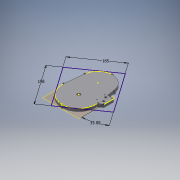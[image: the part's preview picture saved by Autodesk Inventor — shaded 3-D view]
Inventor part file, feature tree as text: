
AUTODESK INVENTOR PART (.ipt)
format: ipt  version: 2017 (Build 210142000, 142)  size: 453,632 bytes
history: native  units: mm
features: extrude x9, sketch x9, other x7, projected_geometry x6, reference x4, plane x2
ambient origin geometry x8: Origin, YZ Plane, XZ Plane, XY Plane, X Axis, Y Axis, Z Axis, Center Point
bodies: Solid1 (feature_tree)
feature tree (37):
  plane  "Work Plane1"
  extrude  "Extrusion1"  Depth=55.0mm
  extrude  "Extrusion2"  Depth=10.0mm TaperAngle=0.0deg
  extrude  "Extrusion3"  Depth=2.0mm TaperAngle=0.0deg
  extrude  "Extrusion5"  Depth=80.0mm
  extrude  "Extrusion6"  Depth=8.0mm
  sketch  "Sketch7"  dims[d12=40.0mm d13=12.0mm]
  extrude  "Extrusion7"  Depth=12.0mm
  extrude  "Extrusion8"  Depth=10.0mm TaperAngle=0.0deg
  extrude  "Extrusion9"  Depth=10.0mm
  sketch  "Sketch9"  dims[d24=10.0mm d25=0.0mm d26=3.81mm]
  plane  "Work Plane2"
  extrude  "Extrusion10"  Depth=10.0mm TaperAngle=0.0deg
  sketch  "Sketch10"  dims[d27=8.0mm d28=10.0mm d29=0.0mm d30=10.0mm d31=0.0mm d32=2.794mm d33=4.0mm d34=33.0mm d35=28.0mm d36=10.0mm d37=0.0mm d38=30.0deg d39=10.0mm d40=0.0mm d41=198.0mm d42=185.0mm d43=6.108652mm d44=13.5mm]
  sketch  "Sketch1"  dims[d0=65.0mm d1=55.0mm]
  reference  "Reference1"
  reference  "Reference2"
  reference  "Reference3"
  reference  "Reference4"
  sketch  "Sketch2"  dims[d2=5.0mm d3=10.0mm d4=0.0mm]
  projected_geometry  "Projected Loop1"
  sketch  "Sketch3"  dims[d5=13.5mm d6=2.0mm d7=0.0mm]
  projected_geometry  "Projected Loop2"
  sketch  "Sketch5"  dims[d8=80.0mm d9=20.0mm]
  sketch  "Sketch6"  dims[d10=3.490659mm d11=8.0mm]
  projected_geometry  "Projected Loop3"
  projected_geometry  "Projected Loop4"
  sketch  "Sketch8"  dims[d14=10.0mm d15=0.0mm d22=10.0mm d23=0.0mm]
  projected_geometry  "Projected Loop5"
  projected_geometry  "Projected Loop6"
  parser-record x1  (decoder bookkeeping rows leaked as tree rows — omitted from the tree; the rows remain in map.json)
  other  "gearbox.iam"
  other  "6003 bearing:4"
  other  "6003 bearing:8"
  other  "Spur Gears:1"
  other  "Spur Gear2:1"
  other  "Spur Gears:3"
note: 1 file-system path scrubbed to <path> (originals preserved in map.json)
